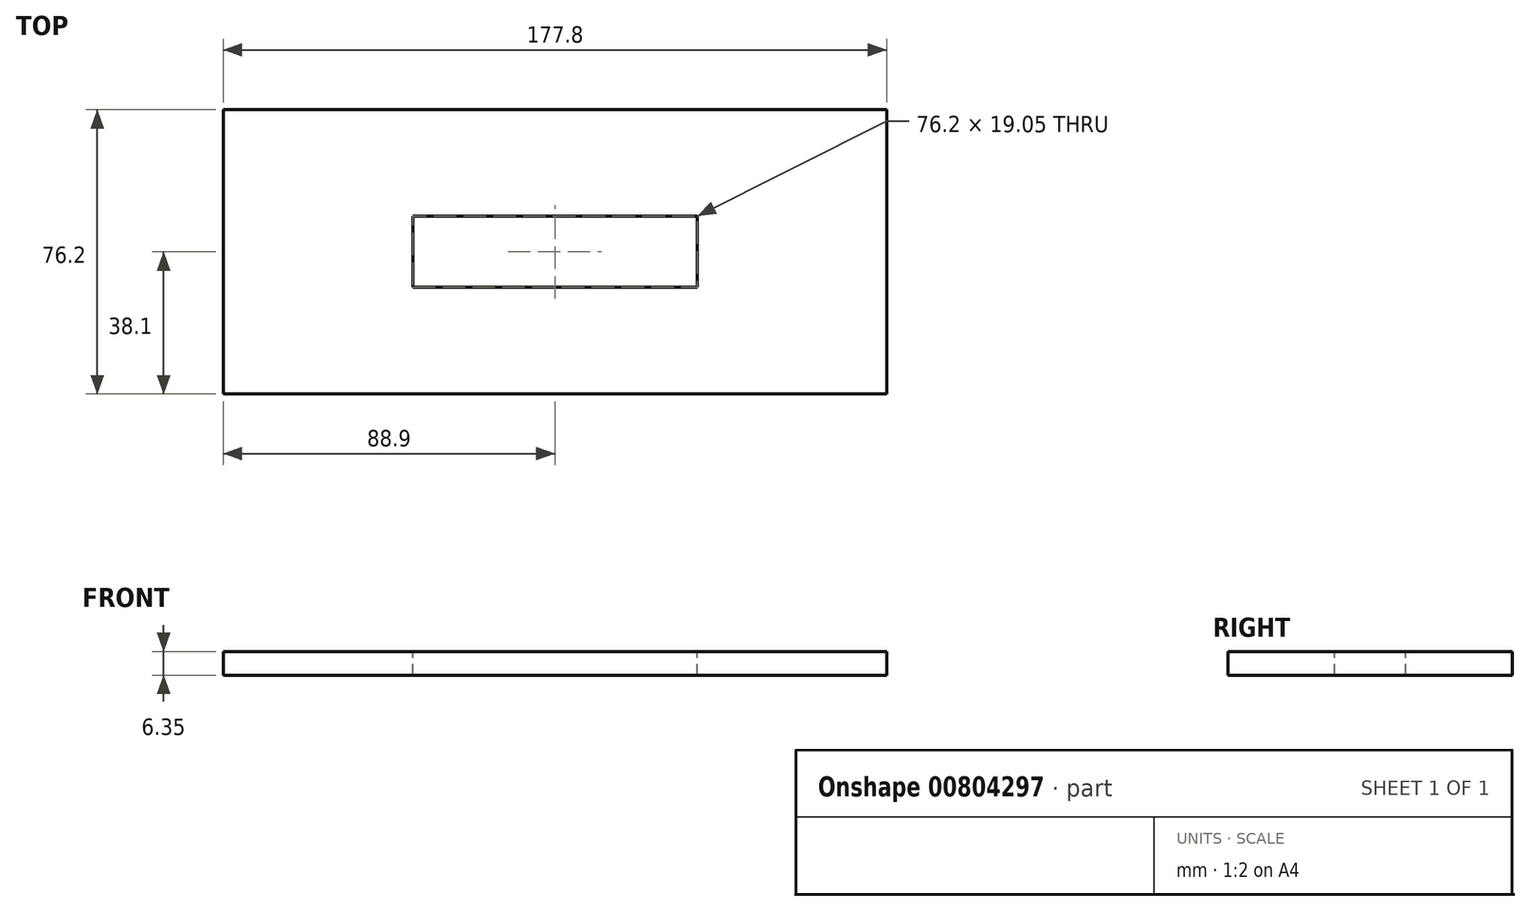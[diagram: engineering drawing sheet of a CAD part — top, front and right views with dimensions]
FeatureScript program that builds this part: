
annotation { "Feature Type Name" : "Feature", "Feature Type Description" : "" }
export const myFeature = defineFeature(function(context is Context, id is Id, definition is map)
    precondition{}
    {
        {
            var Q0;
            Q0=qCreatedBy(makeId("Top.planeOp"),FACE);
            var sketch = newSketch(context, id + "F0", { "sketchPlane" : qUnion([Q0])});
            skLineSegment(sketch, "E0.bottom", {"start": v(-88.9, 38.1) * mm, "end": v(88.9, 38.1) * mm});
            skLineSegment(sketch, "E0.top", {"start": v(-88.9, -38.1) * mm, "end": v(88.9, -38.1) * mm});
            skLineSegment(sketch, "E0.left", {"start": v(-88.9, 38.1) * mm, "end": v(-88.9, -38.1) * mm});
            skLineSegment(sketch, "E0.right", {"start": v(88.9, 38.1) * mm, "end": v(88.9, -38.1) * mm});
            skPoint(sketch, "E1.2.internal.snap0", {"position": v(-88.9, 0) * mm});
            skLineSegment(sketch, "E2.bottom", {"start": v(-38.1, 9.52) * mm, "end": v(38.1, 9.52) * mm});
            skLineSegment(sketch, "E2.top", {"start": v(-38.1, -9.52) * mm, "end": v(38.1, -9.52) * mm});
            skLineSegment(sketch, "E2.left", {"start": v(-38.1, 9.52) * mm, "end": v(-38.1, -9.52) * mm});
            skLineSegment(sketch, "E2.right", {"start": v(38.1, 9.52) * mm, "end": v(38.1, -9.52) * mm});
            skPoint(sketch, "E2.middle", {"position": v(0, 0) * mm});
            skSolve(sketch);
        }
        {
            var Q0;
            Q0=makeQuery(id+"F0.imprint","IMPRINT",FACE,{"disambiguationData":[TD([[makeQuery(id+"F0.imprint","IMPRINT",EDGE,{"derivedFrom":sQuery(id+"F0.wireOp",EDGE,"E0.bottom")}),-1.0]])]});
            extrude(context, id + "F1", {"entities" : qUnion([Q0]), "oppositeDirection" : true, "depth" : 6.35 * mm, "offsetDistance" : 25.4 * mm});
        }
    });
